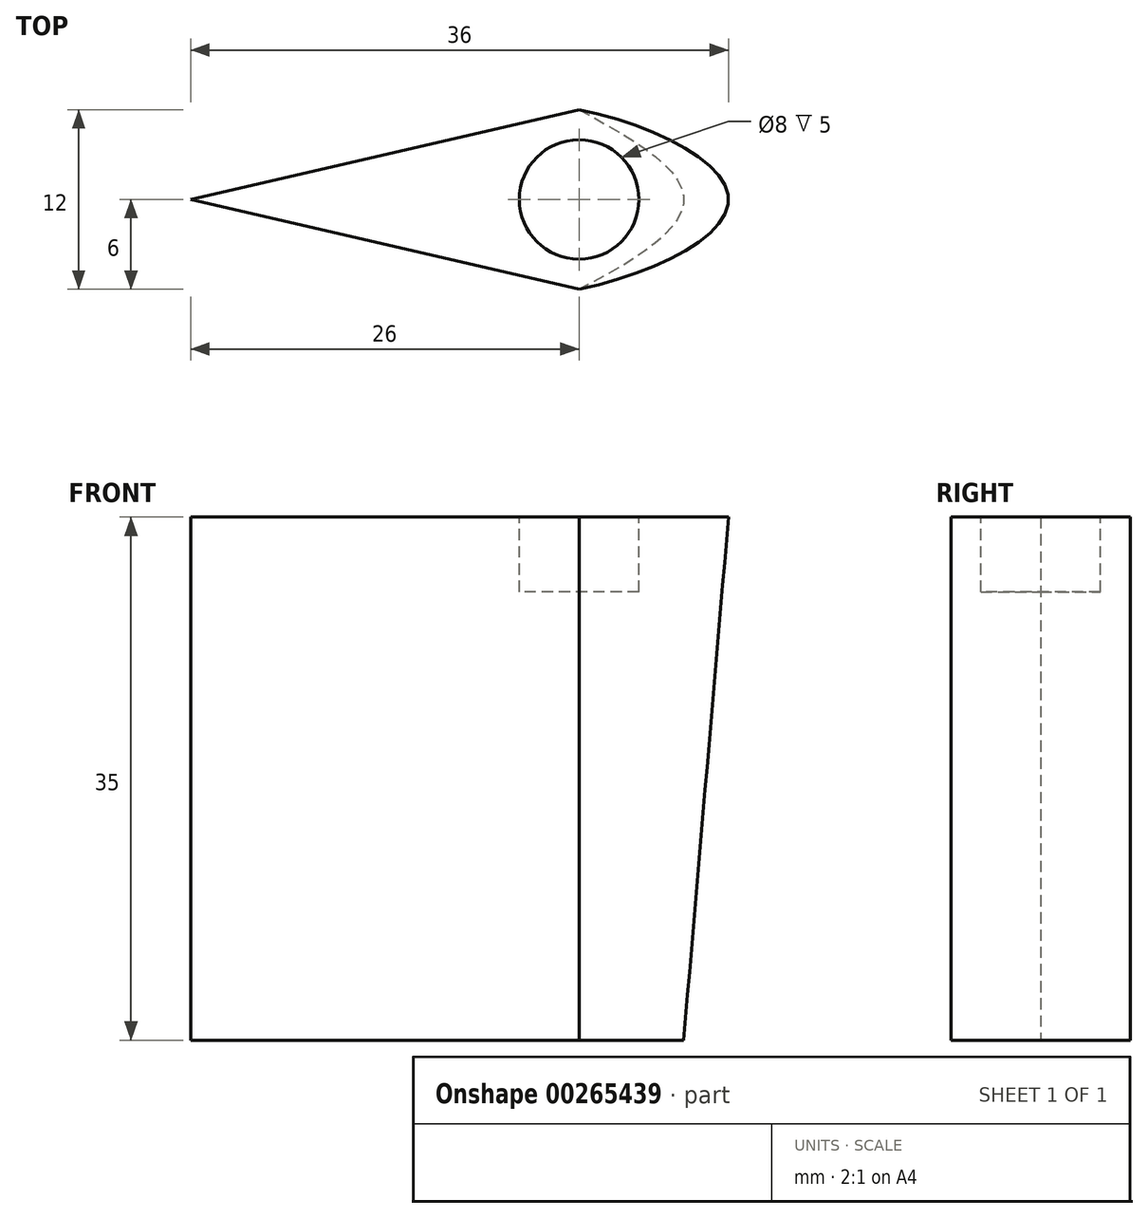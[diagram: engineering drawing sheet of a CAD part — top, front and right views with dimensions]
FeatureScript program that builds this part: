
annotation { "Feature Type Name" : "Feature", "Feature Type Description" : "" }
export const myFeature = defineFeature(function(context is Context, id is Id, definition is map)
    precondition{}
    {
        {
            var Q0;
            Q0=qCreatedBy(makeId("Top.planeOp"),FACE);
            var sketch = newSketch(context, id + "F0", { "sketchPlane" : qUnion([Q0])});
            skLineSegment(sketch, "E0", {"start": v(-26, 0) * mm, "end": v(0, 6) * mm});
            skLineSegment(sketch, "E1", {"start": v(-26, 0) * mm, "end": v(0, -6) * mm});
            skFitSpline(sketch, "E2", {"points": [v(0, 6) * mm, v(10, 0) * mm, v(0, -6) * mm], "startDerivative": vector(29.7, -6) * mm, "endDerivative": vector(-29.94, -6) * mm});
            skPoint(sketch, "E3.middle", {"position": v(0, 0) * mm});
            skSolve(sketch);
        }
        {
            var Q0;
            Q0=qCreatedBy(makeId("Top.planeOp"),FACE);
            cPlane(context, id + "F1", {"entities" : qUnion([Q0]), "cplaneType" : CPlaneType.OFFSET, "offset" : 35 * mm, "oppositeDirection" : true, "width" : 150 * mm, "height" : 150 * mm});
        }
        {
            var Q0;
            Q0=qCreatedBy(id+"F1.planeOp",FACE);
            var sketch = newSketch(context, id + "F2", { "sketchPlane" : qUnion([Q0])});
            skLineSegment(sketch, "E4", {"start": v(-26, 0) * mm, "end": v(0, 6) * mm});
            skLineSegment(sketch, "E5", {"start": v(-26, 0) * mm, "end": v(0, -6) * mm});
            skFitSpline(sketch, "E6", {"points": [v(0, 6) * mm, v(7, 0) * mm, v(0, -6) * mm], "startDerivative": vector(22.88, -12.06) * mm, "endDerivative": vector(-22.94, -11.4) * mm});
            skSolve(sketch);
        }
        {
            var Q0;
            Q0=makeQuery(id+"F0.imprint","IMPRINT",FACE,{"disambiguationData":[TD([[makeQuery(id+"F0.imprint","IMPRINT",EDGE,{"derivedFrom":sQuery(id+"F0.wireOp",EDGE,"E0")}),-1.0]])]});
            var Q1;
            Q1=makeQuery(id+"F2.imprint","IMPRINT",FACE,{"disambiguationData":[TD([[makeQuery(id+"F2.imprint","IMPRINT",EDGE,{"derivedFrom":sQuery(id+"F2.wireOp",EDGE,"E4")}),-1.0]])]});
            loft(context, id + "F3", {"sheetProfilesArray" : [{ "sheetProfileEntities" : qUnion([Q0]) }, { "sheetProfileEntities" : qUnion([Q1]) }]});
        }
        {
            var Q0;
            Q0=makeQuery(id+"F3.opLoft","CAP_FACE",FACE,{"disambiguationData":[OSD([makeQuery(id+"F0.imprint","IMPRINT",FACE,{"disambiguationData":[TD([[makeQuery(id+"F0.imprint","IMPRINT",EDGE,{"derivedFrom":sQuery(id+"F0.wireOp",EDGE,"E0")}),-1.0]])]})])],"isStart":true});
            var sketch = newSketch(context, id + "F4", { "sketchPlane" : qUnion([Q0])});
            skCircle(sketch, "E7", {"center": v(0, 0) * mm, "radius": 4 * mm});
            skPoint(sketch, "E7.first.point", {"position": v(0, 4) * mm});
            skPoint(sketch, "E7.second.point", {"position": v(-4, 0) * mm});
            skPoint(sketch, "E7.third.point", {"position": v(0, -4) * mm});
            skSolve(sketch);
        }
        {
            var Q0;
            Q0 = qSketchRegion(id + "F4", true);
            extrude(context, id + "F5", {"entities" : qUnion([Q0]), "operationType" : NewBodyOperationType.REMOVE, "oppositeDirection" : true, "depth" : 5 * mm});
        }
    });
